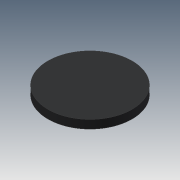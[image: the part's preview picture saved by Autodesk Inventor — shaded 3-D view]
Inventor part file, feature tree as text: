
AUTODESK INVENTOR PART (.ipt)
format: ipt  version: 2020.3 (Build 243373000, 373)  size: 88,064 bytes
history: native  units: in
note: dims shown in document units (in); Inventor stores cm internally (conversion verified against a paired STEP export)
features: extrude x1, sketch x1
ambient origin geometry x8: Origin, YZ Plane, XZ Plane, XY Plane, X Axis, Y Axis, Z Axis, Center Point
bodies: Solid1 (feature_tree)
feature tree (2):
  extrude  "Extrusion1"  Depth=0.25in TaperAngle=0.0deg
  sketch  "Sketch1"  dims[d0=2.5in d1=0.25in d2=0.0in]
